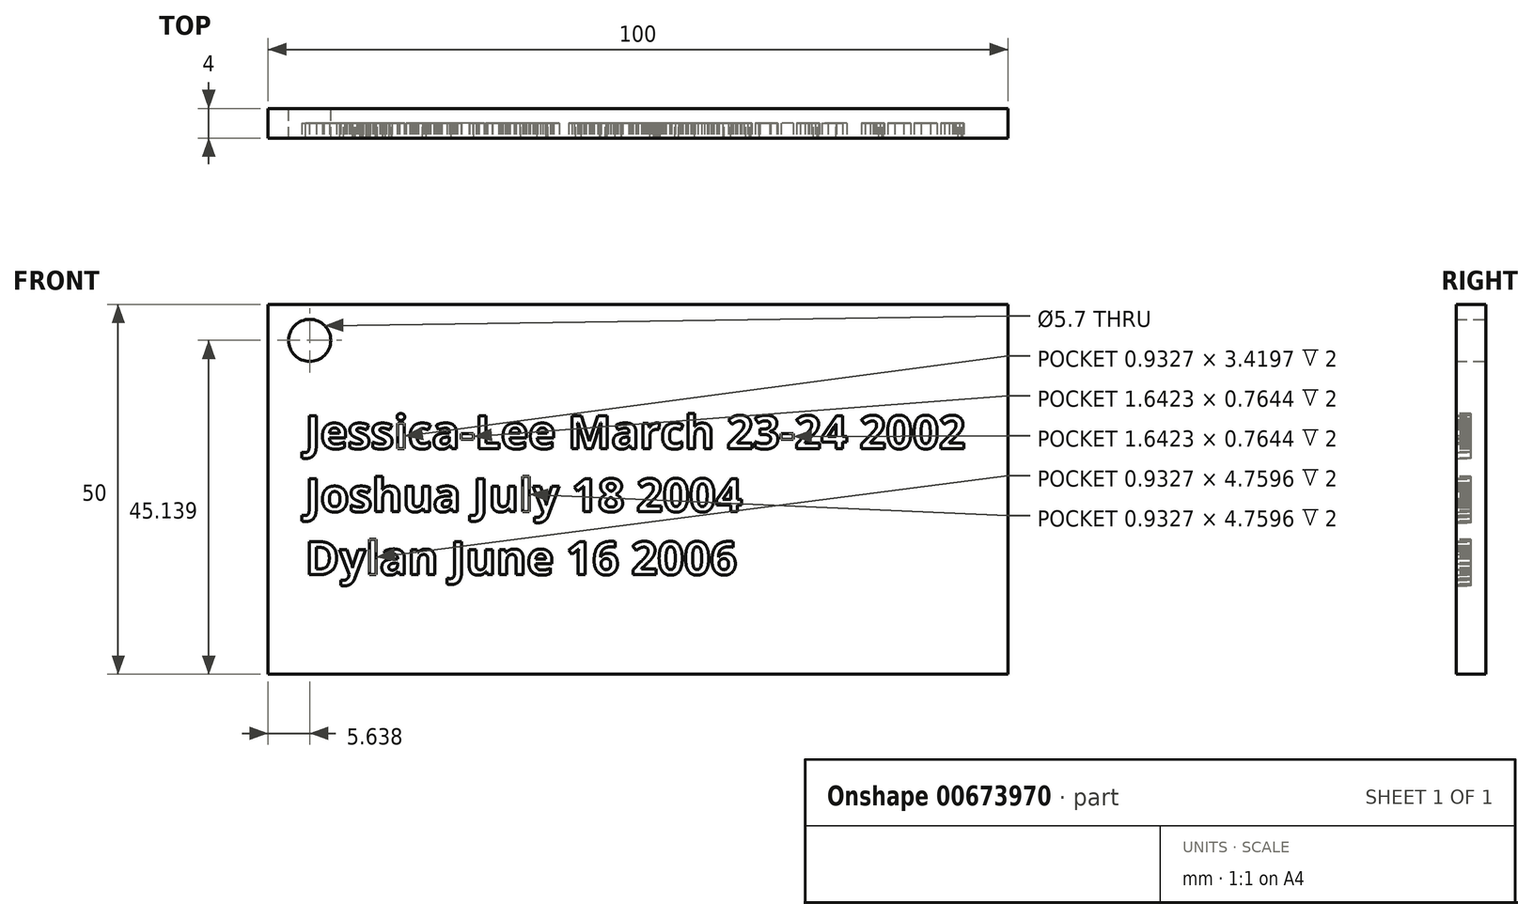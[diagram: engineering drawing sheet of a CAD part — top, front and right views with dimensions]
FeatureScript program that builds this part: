
annotation { "Feature Type Name" : "Feature", "Feature Type Description" : "" }
export const myFeature = defineFeature(function(context is Context, id is Id, definition is map)
    precondition{}
    {
        {
            var Q0;
            Q0=qCreatedBy(makeId("Front.planeOp"),FACE);
            var sketch = newSketch(context, id + "F0", { "sketchPlane" : qUnion([Q0])});
            skLineSegment(sketch, "E0.bottom", {"start": v(50, 25) * mm, "end": v(-50, 25) * mm});
            skLineSegment(sketch, "E0.top", {"start": v(50, -25) * mm, "end": v(-50, -25) * mm});
            skLineSegment(sketch, "E0.left", {"start": v(50, 25) * mm, "end": v(50, -25) * mm});
            skLineSegment(sketch, "E0.right", {"start": v(-50, 25) * mm, "end": v(-50, -25) * mm});
            skPoint(sketch, "E0.middle", {"position": v(0, 0) * mm});
            skCircle(sketch, "E1", {"center": v(-44.36, 20.14) * mm, "radius": 2.85 * mm});
            skSolve(sketch);
        }
        {
            var Q0;
            Q0=makeQuery(id+"F0.imprint","IMPRINT",FACE,{"disambiguationData":[TD([[makeQuery(id+"F0.imprint","IMPRINT",EDGE,{"derivedFrom":sQuery(id+"F0.wireOp",EDGE,"E0.bottom")}),1.0]])]});
            extrude(context, id + "F1", {"entities" : qUnion([Q0]), "depth" : 4 * mm, "offsetDistance" : 25 * mm});
        }
        {
            var Q0;
            Q0=makeQuery(id+"F1.opExtrude","CAP_FACE",FACE,{"disambiguationData":[OSD([sQuery(id+"F0.wireOp",EDGE,"E0.bottom"),sQuery(id+"F0.wireOp",EDGE,"E0.top"),sQuery(id+"F0.wireOp",EDGE,"E0.left"),sQuery(id+"F0.wireOp",EDGE,"E0.right"),sQuery(id+"F0.wireOp",EDGE,"E1")])],"isStart":false});
            var sketch = newSketch(context, id + "F2", { "sketchPlane" : qUnion([Q0])});
            skText(sketch, "E2", { "text": "Jessica-Lee March 23-24 2002\nJoshua July 18 2004\nDylan June 16 2006", "fontName": "OpenSans-Bold.ttf"});
            const initialGuessF2  = {"E2": [-0.045, 0.00549, 1, 0, 0.00451]};
            skSetInitialGuess(sketch, initialGuessF2);
            skSolve(sketch);
        }
        {
            var Q0;
            Q0 = qSketchRegion(id + "F2", true);
            extrude(context, id + "F3", {"entities" : qUnion([Q0]), "operationType" : NewBodyOperationType.REMOVE, "oppositeDirection" : true, "depth" : 2 * mm, "offsetDistance" : 25 * mm});
        }
    });
